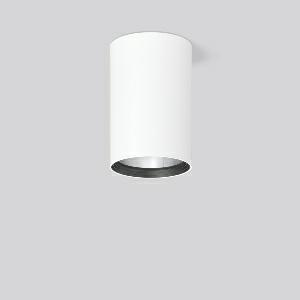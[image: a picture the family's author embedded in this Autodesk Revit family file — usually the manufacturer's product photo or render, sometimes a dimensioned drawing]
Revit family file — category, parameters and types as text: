
# Revit family: heledon_maxi_a_931245_002_2_9dcb
name_source: partatom
category: Lighting Fixtures
units: mm (PartAtom-declared; Revit-internal decimal feet)

## family parameters
Cut with Voids When Loaded = No
Host = Face
Light Source = No
Part Type = Normal
Room Calculation Point = No
Round Connector Dimension = Use Diameter
Shared = No

## types (1)
- HELEDON maxi A (1 x LED Modul 927 bakery, 3400 lm, 2700)
    Apparent Load = 33 VA
    Approval mark = CE
    CIE Flux Codes = 100 100 100 100 100
    Color Rendering = 90
    Color Temperature = 2700
    Default Elevation = 1800 mm
    Description = Series: HELEDON maxi
Cylindrical surface-mounted downlight. Housing: die-cast aluminium, powder-coated. Internal ceiling frame polycarbonate with bayonet mounting. Black plastic ring and recessed LED to prevent glare from the side. Optical assembly with reflector made of MIRO-Silver with 98% total light reflection for outstanding efficiency - can be changed without tools. Special LED for illumination of pastries included. Suitable for Ceiling mounting. Easy installation with a separate ceiling frame with bayonet mounting and plug connection. Driver integrated. Connected via plug-in connector. High quality converter without flickering and stroboscopic effect. The following accessories can be mounted without use of tools: interchangeable lenses, decorative glasses, honeycomb louvre, clear and frosted diffusers, white interchangeable plastic ring. 
Colour: traffic white, matt (RAL 9016)
Diameter: 123 mm
Height: 183 mm
Lamp: LED
Socket: without socket
Colour temperature: bakery
Colour rendering index (CRI): 97
System power: 33 W
Rated luminous flux: 3400 lm
Luminous efficiency: 103 lm/W
Control gear: Regulated power supply
Protection class: I
Type of protection: IP 20
    Height = 183 mm
    Lamp = 1 x LED Modul 927 bakery
    Lamp Light Flux = 3400 lm
    Lamp count = 1
    Length = 123 mm
    Lifetime = 50000 h
    Luminous efficacy = 103 lm/W
    Manufacturer = RZB
    ModVariant = No
    Model = 931245.002.2
    Mounting Place = Ceiling
    Mounting Type = Surface mounted
    Number of Poles = 1
    OnlyDefault = Yes
    Power Factor = 1
    Product Name = HELEDON maxi A
    Product group = Surface mounted downlights
    ProductGroupID = 302
    Protection Class = Protection class I
    Protection Degree = IP 20
    RLX_Detail_Level = 1
    RLX_Emergency_Light_Flux = 0 lm
    RLX_Emergency_Type = 0
    RLX_Emergency_Type_DB = No
    RlxData = <blob elided: 97229 chars, md5=212082fc>
    Socket = socket
    Standby Power = 0 W
    System Light Flux = 3400 lm
    System Power = 33 W
    Type Comments = Product without accessories
    Type Image = 931192.002.jpg
    URL = http://relux.com
    VarID = ---
    Voltage = 230 V
    Voltage Range = 220-240 V
    Weight = 0.00 kg
    Width = 0 mm  [stored 0 ft]

note: [stored X ft] marks values corroborated as IEEE doubles in the binary element streams (Revit-internal decimal feet)

## geometry (parser evidence)
native form markers: Blend x4, Sweep x11
no freeform markers — native parametric forms only
